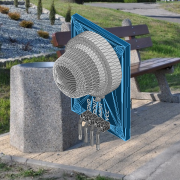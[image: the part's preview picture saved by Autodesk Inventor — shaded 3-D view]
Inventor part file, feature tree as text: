
AUTODESK INVENTOR PART (.ipt)
format: ipt  version: 2021 (Build 250183000, 183)  size: 327,680 bytes
history: native  units: mm
features: extrude x1, sketch x1, other x1
ambient origin geometry x8: Origin, YZ Plane, XZ Plane, XY Plane, X Axis, Y Axis, Z Axis, Center Point
bodies: Solid1 (feature_tree)
feature tree (3):
  extrude  "Extrusion1"  [1 undecoded]
  sketch  "Sketch1"  dims[d0=0.2mm d1=0.0mm]
  other  "MeshFeature1"
note: 1 required parameter value undecoded (feature->parameter linkage not recoverable at this tier; creation-order binding heuristic only, values carry confidence <= 0.55)
